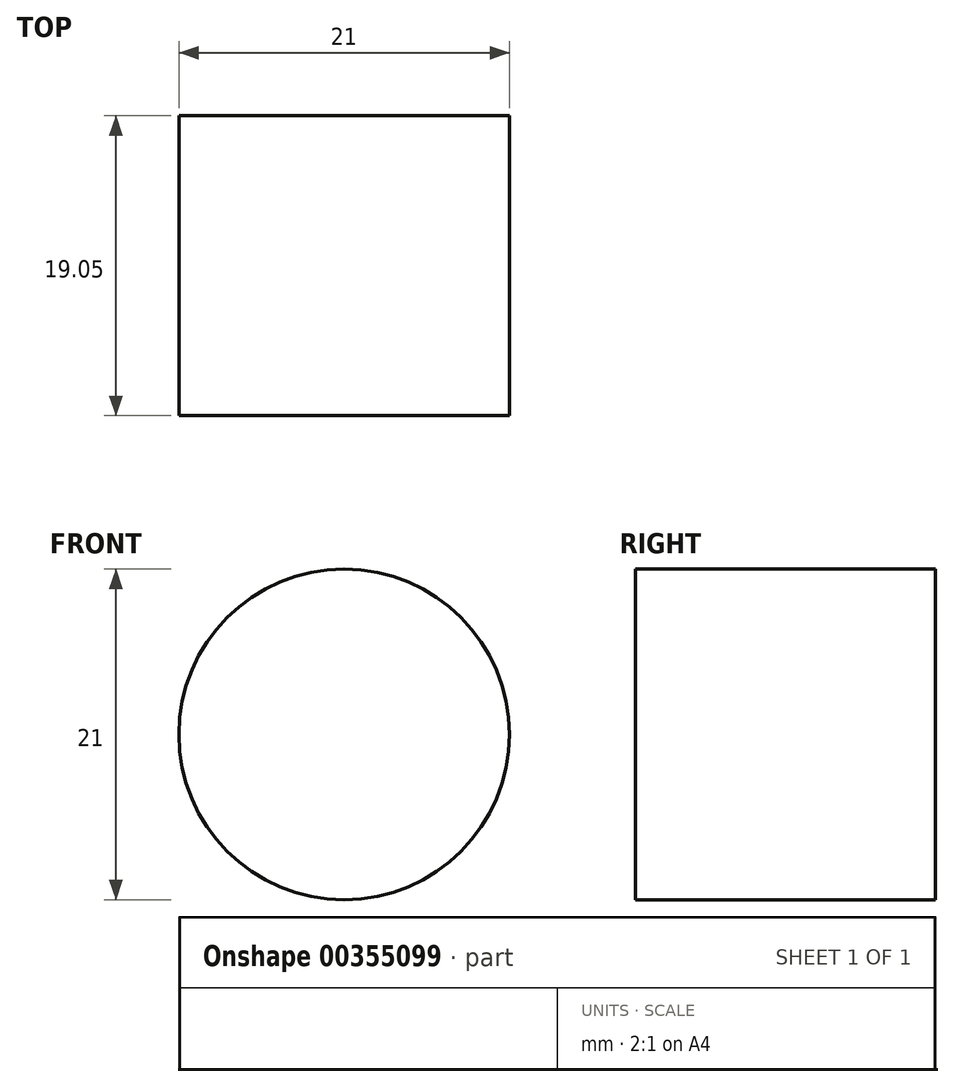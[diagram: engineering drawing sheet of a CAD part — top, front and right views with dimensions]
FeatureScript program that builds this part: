
annotation { "Feature Type Name" : "Feature", "Feature Type Description" : "" }
export const myFeature = defineFeature(function(context is Context, id is Id, definition is map)
    precondition{}
    {
        {
            var Q0;
            Q0=qCreatedBy(makeId("Front.planeOp"),FACE);
            var sketch = newSketch(context, id + "F0", { "sketchPlane" : qUnion([Q0])});
            skCircle(sketch, "E0", {"center": v(0, 0) * mm, "radius": 10.5 * mm});
            skSolve(sketch);
        }
        {
            var Q0;
            Q0 = qSketchRegion(id + "F0", true);
            extrude(context, id + "F1", {"entities" : qUnion([Q0]), "depth" : 19.05 * mm});
        }
    });
